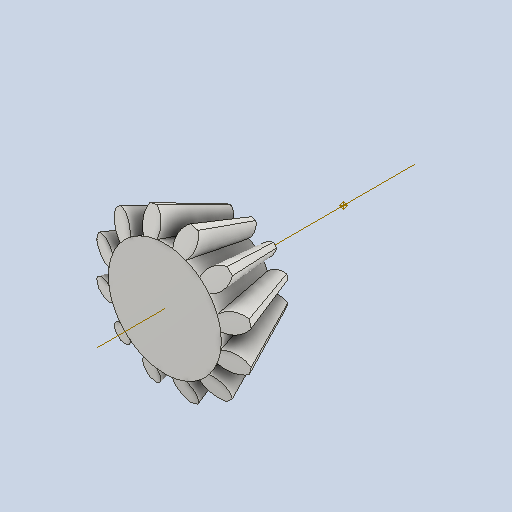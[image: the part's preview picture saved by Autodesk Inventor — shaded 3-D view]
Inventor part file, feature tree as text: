
AUTODESK INVENTOR PART (.ipt)
format: ipt  version: 2022 (Build 260153000, 153)  size: 461,824 bytes
history: native  units: in
note: dims shown in document units (in); Inventor stores cm internally (conversion verified against a paired STEP export)
features: other x30, sketch x1
ambient origin geometry x8: Origin, YZ Plane, XZ Plane, XY Plane, X Axis, Y Axis, Z Axis, Center Point
bodies: Solid1 (feature_tree)
feature tree (31):
  other  "Bevel Gear1"
  other  "Solid1::Bevel Gear1"
  other  "TaggingFeature1"
  other  "Teeth Body Sketch"
  other  "Start Sketch"
  other  "End Sketch"
  other  "End Sketch Right"
  other  "End Sketch Left"
  other  "Body Sketch"
  sketch  "Sketch6"  dims[d0=0.3937in d48=0.0in d49=0.0in d50=90.0deg d52=0.0in d53=0.0in d54=0.0in]
  other  "3D Sketch Right"
  other  "3D Sketch Left"
  other  "Mesh Plane"
  other  "Top Plane"
  other  "Mesh Plane2"
  other  "Tooth Plane"
  other  "End Plane"
  other  "End Plane Right"
  other  "End Plane Left"
  other  "Z Axis_1"
  other  "Top Point"
  other  "Start Point"
  other  "End Point"
  other  "Srf1"
  other  "Srf1::Derived"
  other  "Start plane iMate"
  other  "Mesh iMate2"
  other  "Axis Angle iMate"
  other  "Axis iMate"
  other  "Mesh iMate"
  other  "Intersection iMate"
